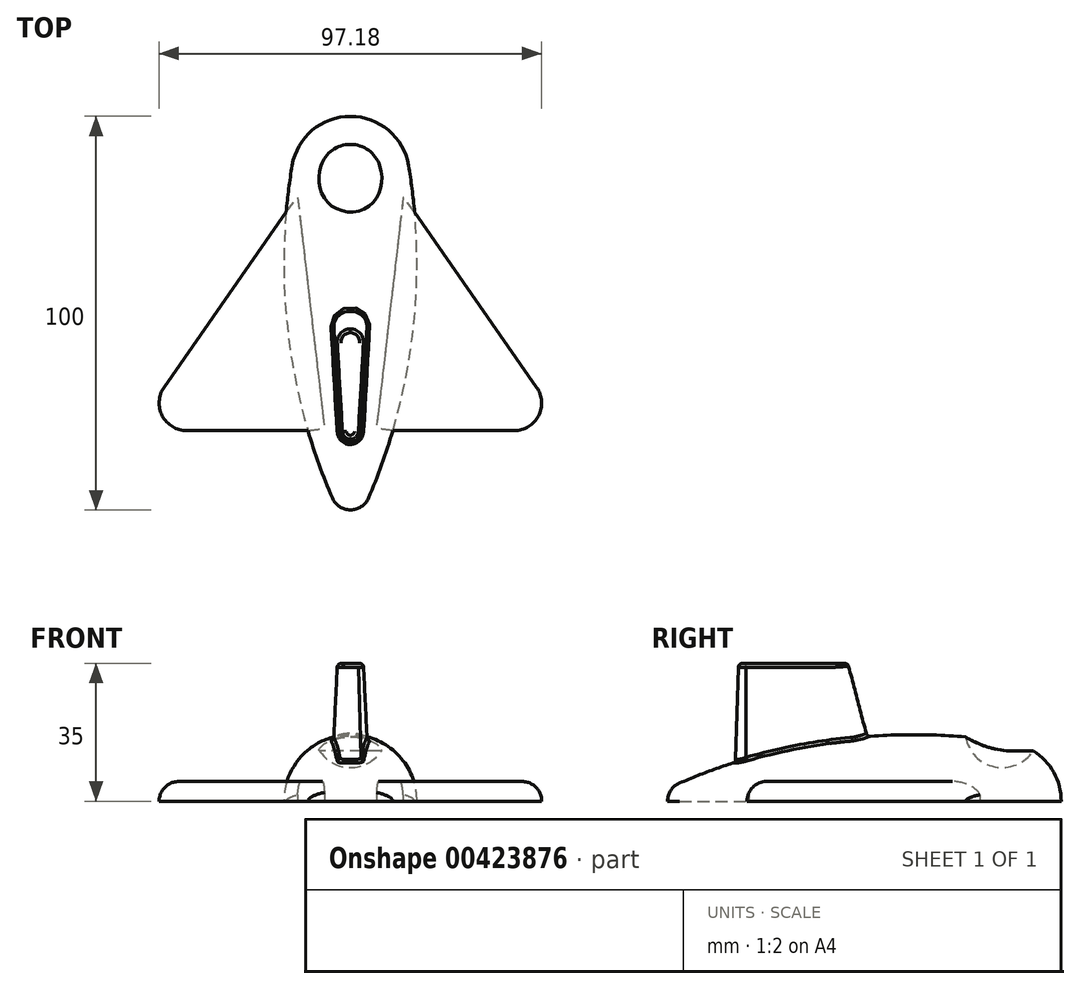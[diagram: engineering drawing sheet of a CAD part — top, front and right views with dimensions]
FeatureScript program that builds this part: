
annotation { "Feature Type Name" : "Feature", "Feature Type Description" : "" }
export const myFeature = defineFeature(function(context is Context, id is Id, definition is map)
    precondition{}
    {
        {
            var Q0;
            Q0=qCreatedBy(makeId("Top.planeOp"),FACE);
            var sketch = newSketch(context, id + "F0", { "sketchPlane" : qUnion([Q0])});
            skLineSegment(sketch, "E0", {"start": v(0, 48.14) * mm, "end": v(0, -51.86) * mm, "construction": true});
            skLineSegment(sketch, "E1", {"start": v(-24.88, 33.14) * mm, "end": v(29.3, 33.14) * mm, "construction": true});
            skArc(sketch, "E2", {"start": v(14.8, 35.64) * mm, "mid": v(9.68, 44.6) * mm, "end": v(0, 48.14) * mm});
            skPoint(sketch, "E2.centerSnap0", {"position": v(2.2, 33.14) * mm});
            skArc(sketch, "E3", {"start": v(0, -51.86) * mm, "mid": v(2.75, -51.04) * mm, "end": v(4.6, -48.85) * mm});
            skArc(sketch, "E4", {"start": v(4.6, -48.85) * mm, "mid": v(15.8, -7.34) * mm, "end": v(14.8, 35.64) * mm});
            skLineSegment(sketch, "E5", {"start": v(0, 48.14) * mm, "end": v(0, -51.86) * mm});
            skLineSegment(sketch, "E6", {"start": v(0, 64.23) * mm, "end": v(0, -74.46) * mm, "construction": true});
            skSolve(sketch);
        }
        {
            var Q0;
            Q0=makeQuery(id+"F0.imprint","IMPRINT",FACE,{"disambiguationData":[TD([[makeQuery(id+"F0.imprint","IMPRINT",EDGE,{"derivedFrom":sQuery(id+"F0.wireOp",EDGE,"E2")}),1.0]])]});
            var Q1;
            Q1=sQuery(id+"F0.wireOp",EDGE,"E6");
            revolve(context, id + "F1", {"entities" : qUnion([Q0]), "axis" : qUnion([Q1]), "revolveType" : RevolveType.ONE_DIRECTION, "angle" : 180 * degree});
        }
        {
            var Q0;
            Q0=qCreatedBy(makeId("Top.planeOp"),FACE);
            var sketch = newSketch(context, id + "F2", { "sketchPlane" : qUnion([Q0])});
            skArc(sketch, "E7", {"start": v(4.99, -2.2) * mm, "mid": v(0, 3.14) * mm, "end": v(-4.99, -2.2) * mm});
            skLineSegment(sketch, "E8", {"start": v(-4.99, -2.2) * mm, "end": v(-3, -32.06) * mm});
            skLineSegment(sketch, "E9", {"start": v(4.99, -2.2) * mm, "end": v(3, -31.86) * mm});
            skArc(sketch, "E10", {"start": v(-3, -32.06) * mm, "mid": v(0.1, -34.87) * mm, "end": v(3, -31.86) * mm});
            skSolve(sketch);
        }
        {
            var Q0;
            Q0=qCreatedBy(makeId("Top.planeOp"),FACE);
            cPlane(context, id + "F3", {"entities" : qUnion([Q0]), "cplaneType" : CPlaneType.OFFSET, "offset" : 35 * mm, "width" : 150 * mm, "height" : 150 * mm});
        }
        {
            var Q0;
            Q0=qCreatedBy(id+"F3.planeOp",FACE);
            var sketch = newSketch(context, id + "F4", { "sketchPlane" : qUnion([Q0])});
            skArc(sketch, "E11", {"start": v(-2, -31.98) * mm, "mid": v(0, -33.86) * mm, "end": v(2, -31.98) * mm});
            skArc(sketch, "E12", {"start": v(3.3, -9.55) * mm, "mid": v(0, -6.06) * mm, "end": v(-3.3, -9.55) * mm});
            skLineSegment(sketch, "E13", {"start": v(3.3, -9.55) * mm, "end": v(2, -31.98) * mm});
            skLineSegment(sketch, "E14", {"start": v(-3.3, -9.55) * mm, "end": v(-2, -31.98) * mm});
            skSolve(sketch);
        }
        {
            var Q0;
            Q0=qCreatedBy(makeId("Right.planeOp"),FACE);
            var sketch = newSketch(context, id + "F5", { "sketchPlane" : qUnion([Q0])});
            skLineSegment(sketch, "E15.0", {"start": v(-9.55, 35) * mm, "end": v(-31.98, 35) * mm});
            skLineSegment(sketch, "E15.1", {"start": v(-2.2, 0) * mm, "end": v(-31.86, 0) * mm});
            skLineSegment(sketch, "E15.2", {"start": v(-34.87, 0) * mm, "end": v(-31.86, 0) * mm});
            skLineSegment(sketch, "E15.3", {"start": v(-2.2, 0) * mm, "end": v(3.14, 0) * mm});
            skLineSegment(sketch, "E15.4", {"start": v(-2.2, 0) * mm, "end": v(-32.06, 0) * mm});
            skLineSegment(sketch, "E15.5", {"start": v(-9.55, 35) * mm, "end": v(-31.98, 35) * mm});
            skLineSegment(sketch, "E15.6", {"start": v(-31.98, 35) * mm, "end": v(-33.86, 35) * mm});
            skLineSegment(sketch, "E15.7", {"start": v(-9.55, 35) * mm, "end": v(-6.06, 35) * mm});
            skPoint(sketch, "E15.8", {"position": v(-20.77, 35) * mm});
            skPoint(sketch, "E15.9", {"position": v(-6.06, 35) * mm});
            skLineSegment(sketch, "E16", {"start": v(-6.06, 35) * mm, "end": v(3.14, 0) * mm});
            skLineSegment(sketch, "E17", {"start": v(-33.86, 35) * mm, "end": v(-34.87, 0) * mm});
            skSolve(sketch);
        }
        {
            var Q1;
            Q1=makeQuery(id+"F4.imprint","IMPRINT",FACE,{"disambiguationData":[TD([[makeQuery(id+"F4.imprint","IMPRINT",EDGE,{"derivedFrom":sQuery(id+"F4.wireOp",EDGE,"E11")}),1.0]])]});
            var Q2;
            Q2 = qSketchRegion(id + "F2", true);
            loft(context, id + "F6", {"operationType" : NewBodyOperationType.ADD, "sheetProfilesArray" : [{ "sheetProfileEntities" : qUnion([Q1]) }, { "sheetProfileEntities" : qUnion([Q2]) }]});
        }
        {
            var Q0;
            Q0=makeQuery(id+"F6.opLoft","CAP_FACE",FACE,{"disambiguationData":[OSD([makeQuery(id+"F4.imprint","IMPRINT",FACE,{"disambiguationData":[TD([[makeQuery(id+"F4.imprint","IMPRINT",EDGE,{"derivedFrom":sQuery(id+"F4.wireOp",EDGE,"E11")}),1.0]])]})])],"isStart":true});
            var Q1;
            Q1=makeQuery(id+"F6.boolean.opBoolean","INTERSECT",EDGE,{"derivedFrom":[makeQuery(id+"F1.opRevolve","SWEPT_FACE",FACE,{"disambiguationData":[OSD([sQuery(id+"F0.wireOp",EDGE,"E4")])]}),makeQuery(id+"F6.opLoft","SWEPT_FACE",FACE,{"disambiguationData":[OSD([sQuery(id+"F2.wireOp",EDGE,"E8"),sQuery(id+"F2.wireOp",EDGE,"E9"),sQuery(id+"F2.wireOp",EDGE,"E10"),sQuery(id+"F4.wireOp",EDGE,"E11"),sQuery(id+"F4.wireOp",EDGE,"E13"),sQuery(id+"F4.wireOp",EDGE,"E14")])]})]});
            fillet(context, id + "F7", {"entities" : qUnion([Q0, Q1]), "radius" : 1 * mm, "tangentPropagation" : true, "allowEdgeOverflow" : false});
        }
        {
            var Q0;
            Q0=qCreatedBy(makeId("Right.planeOp"),FACE);
            var sketch = newSketch(context, id + "F8", { "sketchPlane" : qUnion([Q0])});
            skLineSegment(sketch, "E18.0.1", {"start": v(35.64, 0) * mm, "end": v(-48.85, 0) * mm});
            skLineSegment(sketch, "E18.0.2", {"start": v(-48.85, 0) * mm, "end": v(-48.85, 4.6) * mm});
            skLineSegment(sketch, "E18.0.3", {"start": v(-48.85, 0) * mm, "end": v(35.64, 0) * mm});
            skLineSegment(sketch, "E18.1.0", {"start": v(35.64, 0) * mm, "end": v(48.14, 0) * mm});
            skArc(sketch, "E19", {"start": v(42.58, 18) * mm, "mid": v(33.14, 27.45) * mm, "end": v(23.69, 18) * mm});
            skLineSegment(sketch, "E20", {"start": v(62.65, 18) * mm, "end": v(-72.44, 18) * mm, "construction": true});
            skPoint(sketch, "E18.1.1.end.orphan", {"position": v(35.64, 14.8) * mm});
            skPoint(sketch, "E18.0.0.end.orphan", {"position": v(35.64, 14.8) * mm});
            skLineSegment(sketch, "E21", {"start": v(42.58, 18) * mm, "end": v(23.69, 18) * mm});
            skSolve(sketch);
        }
        {
            var Q0;
            Q0=makeQuery(id+"F8.imprint","IMPRINT",FACE,{"disambiguationData":[TD([[makeQuery(id+"F8.imprint","IMPRINT",EDGE,{"derivedFrom":sQuery(id+"F8.wireOp",EDGE,"E19")}),1.0]])]});
            var Q1;
            Q1=sQuery(id+"F8.wireOp",EDGE,"E20");
            revolve(context, id + "F9", {"operationType" : NewBodyOperationType.REMOVE, "entities" : qUnion([Q0]), "axis" : qUnion([Q1]), "revolveType" : RevolveType.FULL, "oppositeDirection" : true});
        }
        {
            var Q0;
            Q0=qCreatedBy(makeId("Top.planeOp"),FACE);
            var sketch = newSketch(context, id + "F10", { "sketchPlane" : qUnion([Q0])});
            skFitSpline(sketch, "E22.0", {"points": [v(-7.46, 35.64) * mm, v(-7.69, 34.96) * mm, v(-7.92, 33.94) * mm, v(-8, 32.72) * mm, v(-8, 32.02) * mm, v(-7.97, 31.34) * mm, v(-7.86, 30.5) * mm, v(-7.66, 29.67) * mm, v(-7.45, 29.03) * mm, v(-7.2, 28.4) * mm, v(-6.83, 27.67) * mm, v(-6.37, 26.98) * mm, v(-5.94, 26.46) * mm, v(-5.49, 25.98) * mm, v(-4.99, 25.55) * mm, v(-4.44, 25.16) * mm, v(-3.86, 24.8) * mm, v(-3.1, 24.42) * mm, v(-2.12, 24.1) * mm, v(-1.07, 23.89) * mm, v(-0.2, 23.83) * mm, v(0.5, 23.85) * mm, v(1.03, 23.9) * mm, v(1.55, 23.98) * mm, v(2.23, 24.14) * mm, v(2.89, 24.35) * mm, v(3.52, 24.63) * mm, v(4.13, 24.95) * mm, v(4.83, 25.41) * mm, v(5.6, 26.08) * mm, v(6.26, 26.82) * mm, v(6.72, 27.5) * mm, v(7.05, 28.1) * mm, v(7.33, 28.7) * mm, v(7.56, 29.33) * mm, v(7.74, 29.98) * mm, v(7.88, 30.65) * mm, v(8, 31.5) * mm, v(8.02, 32.53) * mm, v(7.94, 33.58) * mm, v(7.76, 34.62) * mm, v(7.57, 35.3) * mm, v(7.46, 35.64) * mm]});
            skArc(sketch, "E22.1", {"start": v(7.46, 35.64) * mm, "mid": v(0, 41) * mm, "end": v(-7.46, 35.64) * mm});
            skLineSegment(sketch, "E23", {"start": v(10.79, -31.7) * mm, "end": v(41.6, -31.7) * mm});
            skArc(sketch, "E24.0", {"start": v(4.6, -48.85) * mm, "mid": v(15.8, -7.34) * mm, "end": v(14.8, 35.64) * mm});
            skLineSegment(sketch, "E25", {"start": v(47.34, -20.7) * mm, "end": v(16.3, 23.84) * mm});
            skPoint(sketch, "E26.visualSharp", {"position": v(55, -31.7) * mm});
            skArc(sketch, "E26.filletArc", {"start": v(41.6, -31.7) * mm, "mid": v(47.8, -27.94) * mm, "end": v(47.34, -20.7) * mm});
            skLineSegment(sketch, "E27", {"start": v(13.4, 27.54) * mm, "end": v(6.6, -31.16) * mm});
            skLineSegment(sketch, "E28", {"start": v(16.3, 23.84) * mm, "end": v(13.4, 27.54) * mm});
            skLineSegment(sketch, "E29", {"start": v(10.79, -31.7) * mm, "end": v(6.6, -31.16) * mm});
            skSolve(sketch);
        }
        {
            var Q0;
            {var subQ0=sQuery(id+"F10.wireOp",EDGE,"E23");Q0=makeQuery(id+"F10.imprint","IMPRINT",FACE,{"disambiguationData":[TD([[makeQuery(id+"F10.imprint","IMPRINT",EDGE,{"derivedFrom":subQ0}),1.0]])]});}
            var Q1;
            Q1=makeQuery(id+"F10.imprint","IMPRINT",FACE,{"disambiguationData":[TD([[makeQuery(id+"F10.imprint","IMPRINT",EDGE,{"derivedFrom":sQuery(id+"F10.wireOp",EDGE,"E27")}),1.0]])]});
            extrude(context, id + "F11", {"entities" : qUnion([Q0, Q1]), "depth" : 5 * mm});
        }
        {
            var Q0;
            Q0=makeQuery(id+"F11.opExtrude","CAP_EDGE",EDGE,{"disambiguationData":[OSD([sQuery(id+"F10.wireOp",EDGE,"E26.filletArc")])],"isStart":false});
            fillet(context, id + "F12", {"entities" : qUnion([Q0]), "radius" : 5 * mm, "tangentPropagation" : true, "allowEdgeOverflow" : false});
        }
        {
            var Q0;
            Q0=makeQuery(id+"F11.opExtrude","SWEPT_BODY",BODY,{"disambiguationData":[OSD([sQuery(id+"F10.wireOp",EDGE,"E23"),sQuery(id+"F10.wireOp",EDGE,"E24.0"),sQuery(id+"F10.wireOp",EDGE,"E25"),sQuery(id+"F10.wireOp",EDGE,"E26.filletArc")])]});
            var Q1;
            Q1=qCreatedBy(makeId("Right.planeOp"),FACE);
            mirror(context, id + "F13", {"entities" : qUnion([Q0]), "mirrorPlane" : qUnion([Q1])});
        }
    });
